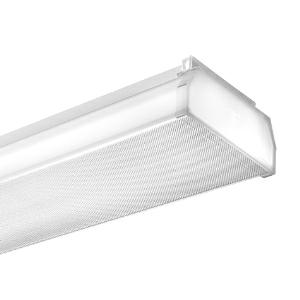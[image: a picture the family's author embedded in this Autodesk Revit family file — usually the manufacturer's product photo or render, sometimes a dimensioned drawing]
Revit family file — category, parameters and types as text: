
# Revit family: 3f_filippi_-_zero_3f_3f_filippi_-_1863_-_03f_14w-840_dali_l620
name_source: partatom
category: Lighting Fixtures
units: mm (PartAtom-declared; Revit-internal decimal feet)

## family parameters
Cut with Voids When Loaded = No
Host = Face
Light Source = No
Part Type = Normal
Room Calculation Point = No
Round Connector Dimension = Use Diameter
Shared = No

## types (1)
- 3F Filippi - Zero 3F (1 x LED, 2014 lm, 16 W, 4000 K)
    Apparent Load = 16 VA
    Approval mark = CE
    CIE Flux Codes = 55 84 94 83 100
    Color Rendering = 80
    Color Temperature = 4000 K
    Control Gear = Electronic transformer
    Default Elevation = 1800 mm
    Description = ILLUMINOTECHNICAL
Luminous efficiency 100% (DLOR 83%, ULOR 17%).
Initial luminous flux of the luminaire 2014 lm.
Controlled symmetric distribution.
Installation Interdistance Transv.D = 1.32 x hu - Long.D = 1.30 x hu.
Average luminance <3000 cd/m² for radial angles >65°.
Tabular UGR (CIE 117 - 4H-8H; S=0.25H; 70/50/20): RUG 18.9 - 17.4.
Beam angle: 99° - 100°.
Luminous efficacy 126 lm/W.
Lifetime (L93/B10): 30000 h. (tq+25°C)
Lifetime (L90/B10): 50000 h. (tq+25°C)
Lifetime (L85/B10): 80000 h. (tq+25°C)
Lifetime (L80/B10): 100000 h. (tq+25°C)
Sudden decreased luminous flux after 50000 hours: 0% (C0).
Photobiological safety in compliance with IEC/TR 62778: RG0 risk exempt, (IEC 62471).
In compliance with IEC/EN 62722-2-1 - IEC/EN 62717 standards.

SOURCE
Linear LED module 14W/840.
Energy efficiency class (UE 2019/2020 - UE 2019/2015): D.
CIE 13.3 Colour rendering index: CRI >80 (R9 <50%).
IES TM-30 Fidelity Index: Rf = 84 Rg = 95.
CCT nominal colour temperature 4000 K.
Colour initial tolerance (MacAdam): SDCM 3.

MECHANICAL
Housing in hot-galvanised steel, painted in white polyester.
Diffuser with differentiated geometry, made of transparent methacrylate (PMMA) with microprismatic finish, anti-glare on the flat part and opal on the side.
Anti-glare opal methacrylate (PMMA) filter for brightness uniformity.
Lighting end caps in methacrylate (PMMA) opal.
Luminaire with limited surface temperature. - D - (EN 60598-2-24)
Dimensions: 620x119 mm, height 64 mm. Weight 1.28 kg.
IP40 protection degree.
Mechanical strength to impacts IK06 (1 joule).
Glow-wire test resistance 650°C.

ELECTRICAL
Halogen Free DALI-2 DATI (Parts 251, 252, 253), PUSH-DIM, electronic wiring 230V-50/60Hz, power factor 0.90 at full load, THD <25%, constant output current, SELV, class I, 1 driver, 1 DALI addresse.
Power of the luminaire 16 W.
ENEC - CE.
SAFE FLICKER: PstLM=<1 and SVM=<0.4 (IEC TR 61547-1 and IEC TR 63158), to ensure a more comfortable and safe light.
Luminaire compliant with EN 60598-2-22 for power supply from a centralised emergency system CPSS (Central Power Supply System), not incorporated in the luminaire - high risk areas excluded. The default power and flux are 100% in AC and 15% in DC.
Ambient temperature from +5°C to +25°C.
Temperature class T6 max 85°C.
Relative humidity UR: <85%.

INSTALLATION
Ceiling / Suspended / Wall.
Thanks to the full compatibility for dimensions and fixing distances, this product becomes the perfect solution for updating existing installations.
All accessories dedicated to this product are available on the Catalog and on our website www.3F-Filippi.com.

APPLICATIONS
Suitable product for food production plants (HACCP), IFS (Food Version 6), BRC (GSFS Food Version 7).
Environments: with VDTs, meeting rooms, offices.
Environments: recreational, transit areas, corridors, schools, stairwells.
Environments where soft diffuse light is required for optimal visual comfort.

LIGHT MANAGEMENT
Recommended minimum setting: 10%.
The luminaire, equipped with (DALI-2 DATI) driver, can be controlled manually with 3F Easy Dim technology or automatically/manually with wired or wireless DALI/D2D control systems.
The D2D driver guarantees interoperability with other devices with the same certification by making the following information available:
Device Data (Part 251), Energy Report (Part 252), Diagnosis & Maintenance (Part 253).
In electrical systems without a regulation system (manual or automatic) and DALI bus, a suitable jumper must be made on the DA-DA terminals of the appliance.

WARNING
Luminaire designed for disposal/recycling at end-of-life.
Replaceable (LED only) light source by a professional. Replaceable control gear by a professional.
    Height = 64 mm
    Lamp = 1 x LED
    Lamp Light Flux = 2014 lm
    Lamp Power = 16 W
    Lamp count = 1
    Length = 620 mm
    Lifetime = 50000 h
    Luminous efficacy = 126 lm/W
    Manufacturer = 3F Filippi
    ModVariant = No
    Model = 3F Filippi - 1863 - 03F 14W-840 DALI L620
    Mounting Place = Ceiling
    Mounting Type = Surface mounted
    Number of Poles = 1
    OnlyDefault = Yes
    Power Factor = 1
    Product Name = 3F Filippi - Zero 3F
    Product group = ceiling mounted luminaire
    ProductGroupID = 3
    Protection Class = Protection class I
    Protection Degree = IP 40
    RLX_Detail_Level = 1
    RLX_Emergency_Light_Flux = 0 lm
    RLX_Emergency_Type = 0
    RLX_Emergency_Type_DB = No
    RlxData = <blob elided: 150337 chars, md5=ffba2490>
    Socket = socket
    Standby Power = 0 W
    System Light Flux = 2014 lm
    System Power = 16 W
    Type Comments = Product without accessories
    Type Image = 3ffilippi_zero_3f.jpg
    URL = http://relux.com
    VarID = ---
    Voltage = 0 V
    Weight = 0.00 kg
    Width = 119 mm

## geometry (parser evidence)
native form markers: Blend x4, Sweep x13
no freeform markers — native parametric forms only
